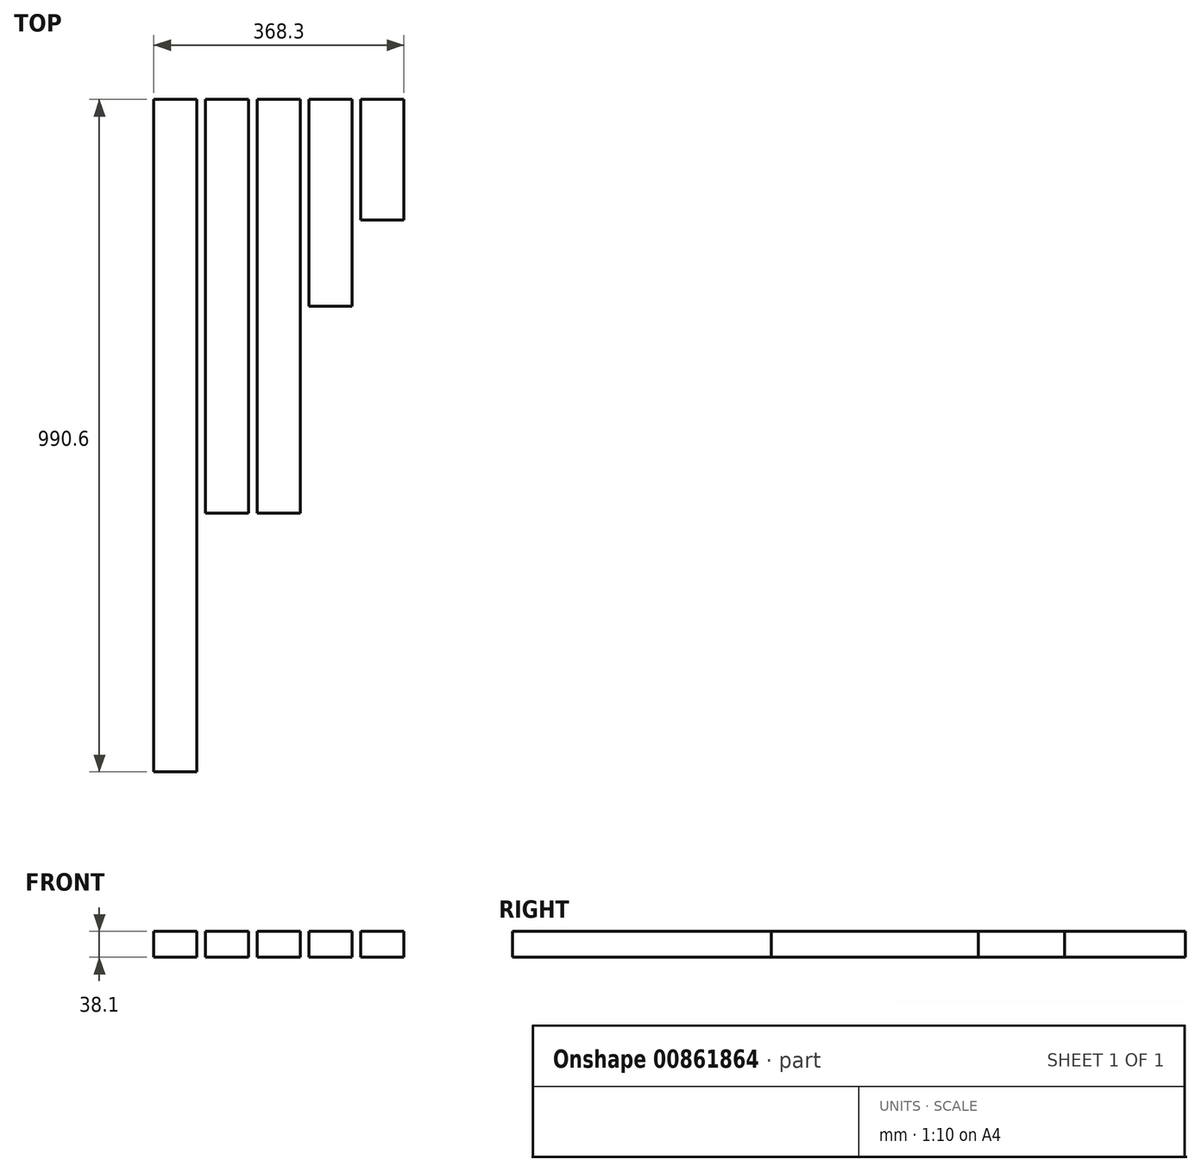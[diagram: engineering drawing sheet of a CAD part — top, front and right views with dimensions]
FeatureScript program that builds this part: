
annotation { "Feature Type Name" : "Feature", "Feature Type Description" : "" }
export const myFeature = defineFeature(function(context is Context, id is Id, definition is map)
    precondition{}
    {
        {
            var Q0;
            Q0=qCreatedBy(makeId("Front.planeOp"),FACE);
            var sketch = newSketch(context, id + "F0", { "sketchPlane" : qUnion([Q0])});
            skLineSegment(sketch, "E0.bottom", {"start": v(31.75, -19.05) * mm, "end": v(-31.75, -19.05) * mm});
            skLineSegment(sketch, "E0.top", {"start": v(31.75, 19.05) * mm, "end": v(-31.75, 19.05) * mm});
            skLineSegment(sketch, "E0.left", {"start": v(31.75, -19.05) * mm, "end": v(31.75, 19.05) * mm});
            skLineSegment(sketch, "E0.right", {"start": v(-31.75, -19.05) * mm, "end": v(-31.75, 19.05) * mm});
            skPoint(sketch, "E0.middle", {"position": v(0, 0) * mm});
            skSolve(sketch);
        }
        {
            var Q0;
            Q0=makeQuery(id+"F0.imprint","IMPRINT",FACE,{"disambiguationData":[TD([[makeQuery(id+"F0.imprint","IMPRINT",EDGE,{"derivedFrom":sQuery(id+"F0.wireOp",EDGE,"E0.bottom")}),-1.0]])]});
            extrude(context, id + "F1", {"entities" : qUnion([Q0]), "depth" : 914.4 * mm, "offsetDistance" : 25.4 * mm});
        }
        {
            var Q0;
            Q0=makeQuery(id+"F1.opExtrude","SWEPT_BODY",BODY,{"disambiguationData":[OSD([sQuery(id+"F0.wireOp",EDGE,"E0.bottom"),sQuery(id+"F0.wireOp",EDGE,"E0.top"),sQuery(id+"F0.wireOp",EDGE,"E0.left"),sQuery(id+"F0.wireOp",EDGE,"E0.right")])]});
            transform(context, id + "F2", {"entities" : qUnion([Q0]), "transformType" : TransformType.TRANSLATION_3D, "dx" : 76.2 * mm, "dy" : 0 * mm, "dz" : 0 * mm, "makeCopy" : true});
        }
        {
            var Q0;
            Q0=makeQuery(id+"F2.opPattern","COPY",FACE,{"derivedFrom":makeQuery(id+"F1.opExtrude","CAP_FACE",FACE,{"disambiguationData":[OSD([sQuery(id+"F0.wireOp",EDGE,"E0.bottom"),sQuery(id+"F0.wireOp",EDGE,"E0.top"),sQuery(id+"F0.wireOp",EDGE,"E0.left"),sQuery(id+"F0.wireOp",EDGE,"E0.right")])],"isStart":false}),"instanceName":"1"});
            extrude(context, id + "F3", {"entities" : qUnion([Q0]), "operationType" : NewBodyOperationType.REMOVE, "oppositeDirection" : true, "depth" : 304.8 * mm, "offsetDistance" : 25.4 * mm});
        }
        {
            var Q0;
            Q0=makeQuery(id+"F2.opPattern","COPY",BODY,{"derivedFrom":makeQuery(id+"F1.opExtrude","SWEPT_BODY",BODY,{"disambiguationData":[OSD([sQuery(id+"F0.wireOp",EDGE,"E0.bottom"),sQuery(id+"F0.wireOp",EDGE,"E0.top"),sQuery(id+"F0.wireOp",EDGE,"E0.left"),sQuery(id+"F0.wireOp",EDGE,"E0.right")])]}),"instanceName":"1"});
            transform(context, id + "F4", {"entities" : qUnion([Q0]), "transformType" : TransformType.TRANSLATION_3D, "dx" : 76.2 * mm, "dy" : 0 * mm, "dz" : 0 * mm, "makeCopy" : true});
        }
        {
            var Q0;
            Q0=makeQuery(id+"F4.opPattern","COPY",FACE,{"derivedFrom":makeQuery(id+"F3.boolean.opBoolean","COPY",FACE,{"derivedFrom":makeQuery(id+"F3.opExtrude","CAP_FACE",FACE,{"disambiguationData":[OSD([sQuery(id+"F0.wireOp",EDGE,"E0.bottom"),sQuery(id+"F0.wireOp",EDGE,"E0.top"),sQuery(id+"F0.wireOp",EDGE,"E0.left"),sQuery(id+"F0.wireOp",EDGE,"E0.right")])],"isStart":false})}),"instanceName":"1"});
            extrude(context, id + "F5", {"entities" : qUnion([Q0]), "operationType" : NewBodyOperationType.REMOVE, "oppositeDirection" : true, "depth" : 304.8 * mm, "offsetDistance" : 25.4 * mm});
        }
        {
            var Q0;
            Q0=makeQuery(id+"F4.opPattern","COPY",BODY,{"derivedFrom":makeQuery(id+"F2.opPattern","COPY",BODY,{"derivedFrom":makeQuery(id+"F1.opExtrude","SWEPT_BODY",BODY,{"disambiguationData":[OSD([sQuery(id+"F0.wireOp",EDGE,"E0.bottom"),sQuery(id+"F0.wireOp",EDGE,"E0.top"),sQuery(id+"F0.wireOp",EDGE,"E0.left"),sQuery(id+"F0.wireOp",EDGE,"E0.right")])]}),"instanceName":"1"}),"instanceName":"1"});
            transform(context, id + "F6", {"entities" : qUnion([Q0]), "transformType" : TransformType.TRANSLATION_3D, "dx" : 76.2 * mm, "dy" : 0 * mm, "dz" : 0 * mm, "makeCopy" : true});
        }
        {
            var Q0;
            Q0=makeQuery(id+"F6.opPattern","COPY",FACE,{"derivedFrom":makeQuery(id+"F5.boolean.opBoolean","COPY",FACE,{"derivedFrom":makeQuery(id+"F5.opExtrude","CAP_FACE",FACE,{"disambiguationData":[OSD([sQuery(id+"F0.wireOp",EDGE,"E0.bottom"),sQuery(id+"F0.wireOp",EDGE,"E0.top"),sQuery(id+"F0.wireOp",EDGE,"E0.left"),sQuery(id+"F0.wireOp",EDGE,"E0.right")])],"isStart":false})}),"instanceName":"1"});
            extrude(context, id + "F7", {"entities" : qUnion([Q0]), "operationType" : NewBodyOperationType.REMOVE, "oppositeDirection" : true, "depth" : 76.2 * mm, "offsetDistance" : 25.4 * mm});
        }
        {
            var Q0;
            Q0=makeQuery(id+"F1.opExtrude","SWEPT_BODY",BODY,{"disambiguationData":[OSD([sQuery(id+"F0.wireOp",EDGE,"E0.bottom"),sQuery(id+"F0.wireOp",EDGE,"E0.top"),sQuery(id+"F0.wireOp",EDGE,"E0.left"),sQuery(id+"F0.wireOp",EDGE,"E0.right")])]});
            transform(context, id + "F8", {"entities" : qUnion([Q0]), "transformType" : TransformType.TRANSLATION_3D, "dx" : -76.2 * mm, "dy" : 0 * mm, "dz" : 0 * mm, "makeCopy" : true});
        }
        {
            var Q0;
            Q0=makeQuery(id+"F8.opPattern","COPY",FACE,{"derivedFrom":makeQuery(id+"F1.opExtrude","CAP_FACE",FACE,{"disambiguationData":[OSD([sQuery(id+"F0.wireOp",EDGE,"E0.bottom"),sQuery(id+"F0.wireOp",EDGE,"E0.top"),sQuery(id+"F0.wireOp",EDGE,"E0.left"),sQuery(id+"F0.wireOp",EDGE,"E0.right")])],"isStart":false}),"instanceName":"1"});
            extrude(context, id + "F9", {"entities" : qUnion([Q0]), "operationType" : NewBodyOperationType.ADD, "depth" : 203.2 * mm, "offsetDistance" : 25.4 * mm});
        }
        {
            var Q0;
            Q0=makeQuery(id+"F9.opExtrude","CAP_FACE",FACE,{"disambiguationData":[OSD([sQuery(id+"F0.wireOp",EDGE,"E0.bottom"),sQuery(id+"F0.wireOp",EDGE,"E0.top"),sQuery(id+"F0.wireOp",EDGE,"E0.left"),sQuery(id+"F0.wireOp",EDGE,"E0.right")])],"isStart":false});
            extrude(context, id + "F10", {"entities" : qUnion([Q0]), "operationType" : NewBodyOperationType.ADD, "depth" : -38.1 * mm, "offsetDistance" : 25.4 * mm});
        }
        {
            var Q0;
            Q0=makeQuery(id+"F9.opExtrude","CAP_FACE",FACE,{"disambiguationData":[OSD([sQuery(id+"F0.wireOp",EDGE,"E0.bottom"),sQuery(id+"F0.wireOp",EDGE,"E0.top"),sQuery(id+"F0.wireOp",EDGE,"E0.left"),sQuery(id+"F0.wireOp",EDGE,"E0.right")])],"isStart":false});
            extrude(context, id + "F11", {"entities" : qUnion([Q0]), "operationType" : NewBodyOperationType.REMOVE, "oppositeDirection" : true, "depth" : 38.1 * mm, "offsetDistance" : 25.4 * mm});
        }
        {
            var Q0;
            Q0=makeQuery(id+"F1.opExtrude","CAP_FACE",FACE,{"disambiguationData":[OSD([sQuery(id+"F0.wireOp",EDGE,"E0.bottom"),sQuery(id+"F0.wireOp",EDGE,"E0.top"),sQuery(id+"F0.wireOp",EDGE,"E0.left"),sQuery(id+"F0.wireOp",EDGE,"E0.right")])],"isStart":false});
            extrude(context, id + "F12", {"entities" : qUnion([Q0]), "operationType" : NewBodyOperationType.REMOVE, "oppositeDirection" : true, "depth" : 304.8 * mm, "offsetDistance" : 25.4 * mm});
        }
        {
            var Q0;
            Q0=makeQuery(id+"F11.boolean.opBoolean","COPY",FACE,{"derivedFrom":makeQuery(id+"F11.opExtrude","CAP_FACE",FACE,{"disambiguationData":[OSD([sQuery(id+"F0.wireOp",EDGE,"E0.bottom"),sQuery(id+"F0.wireOp",EDGE,"E0.top"),sQuery(id+"F0.wireOp",EDGE,"E0.left"),sQuery(id+"F0.wireOp",EDGE,"E0.right")])],"isStart":false})});
            extrude(context, id + "F13", {"entities" : qUnion([Q0]), "operationType" : NewBodyOperationType.REMOVE, "oppositeDirection" : true, "depth" : 88.9 * mm, "offsetDistance" : 25.4 * mm});
        }
        {
            var Q0;
            Q0=makeQuery(id+"F7.boolean.opBoolean","COPY",FACE,{"derivedFrom":makeQuery(id+"F7.opExtrude","CAP_FACE",FACE,{"disambiguationData":[OSD([sQuery(id+"F0.wireOp",EDGE,"E0.bottom"),sQuery(id+"F0.wireOp",EDGE,"E0.top"),sQuery(id+"F0.wireOp",EDGE,"E0.left"),sQuery(id+"F0.wireOp",EDGE,"E0.right")])],"isStart":false})});
            extrude(context, id + "F14", {"entities" : qUnion([Q0]), "operationType" : NewBodyOperationType.REMOVE, "oppositeDirection" : true, "depth" : 50.8 * mm, "offsetDistance" : 25.4 * mm});
        }
    });
